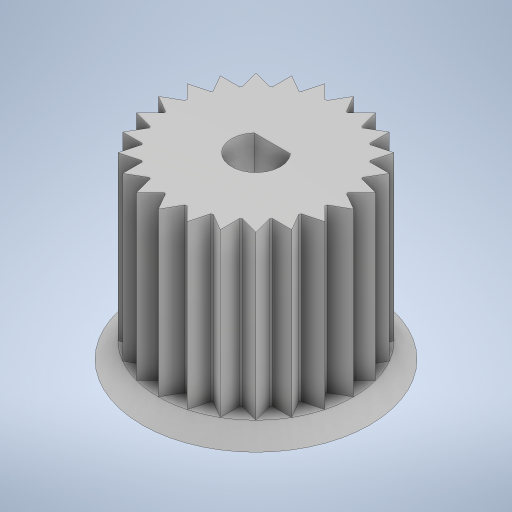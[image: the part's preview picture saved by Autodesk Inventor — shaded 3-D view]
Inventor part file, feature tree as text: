
AUTODESK INVENTOR PART (.ipt)
format: ipt  version: 2023 (Build 270158000, 158)  size: 314,368 bytes
history: mixed  units: in
note: dims shown in document units (in); Inventor stores cm internally (conversion verified against a paired STEP export)
features: other x1, extrude x1, sketch x1, imported_body x1
ambient origin geometry x8: Origin, YZ Plane, XZ Plane, XY Plane, X Axis, Y Axis, Z Axis, Center Point
bodies: Solid1 (imported_parasolid), Body1 (imported_parasolid)
feature tree (4):
  other  "Repaired Geometry1"
  extrude  "Extrusion1"  TaperAngle=0.0deg  [1 undecoded]
  sketch  "Sketch2"  dims[d1=0.0984in d2=0.0in d3=0.0in]
  imported_body  NMx_Import_Brep_tag  [imported B-rep: ~5 faces, bbox_mm=None]
note: 1 required parameter value undecoded (feature->parameter linkage not recoverable at this tier; creation-order binding heuristic only, values carry confidence <= 0.55)
